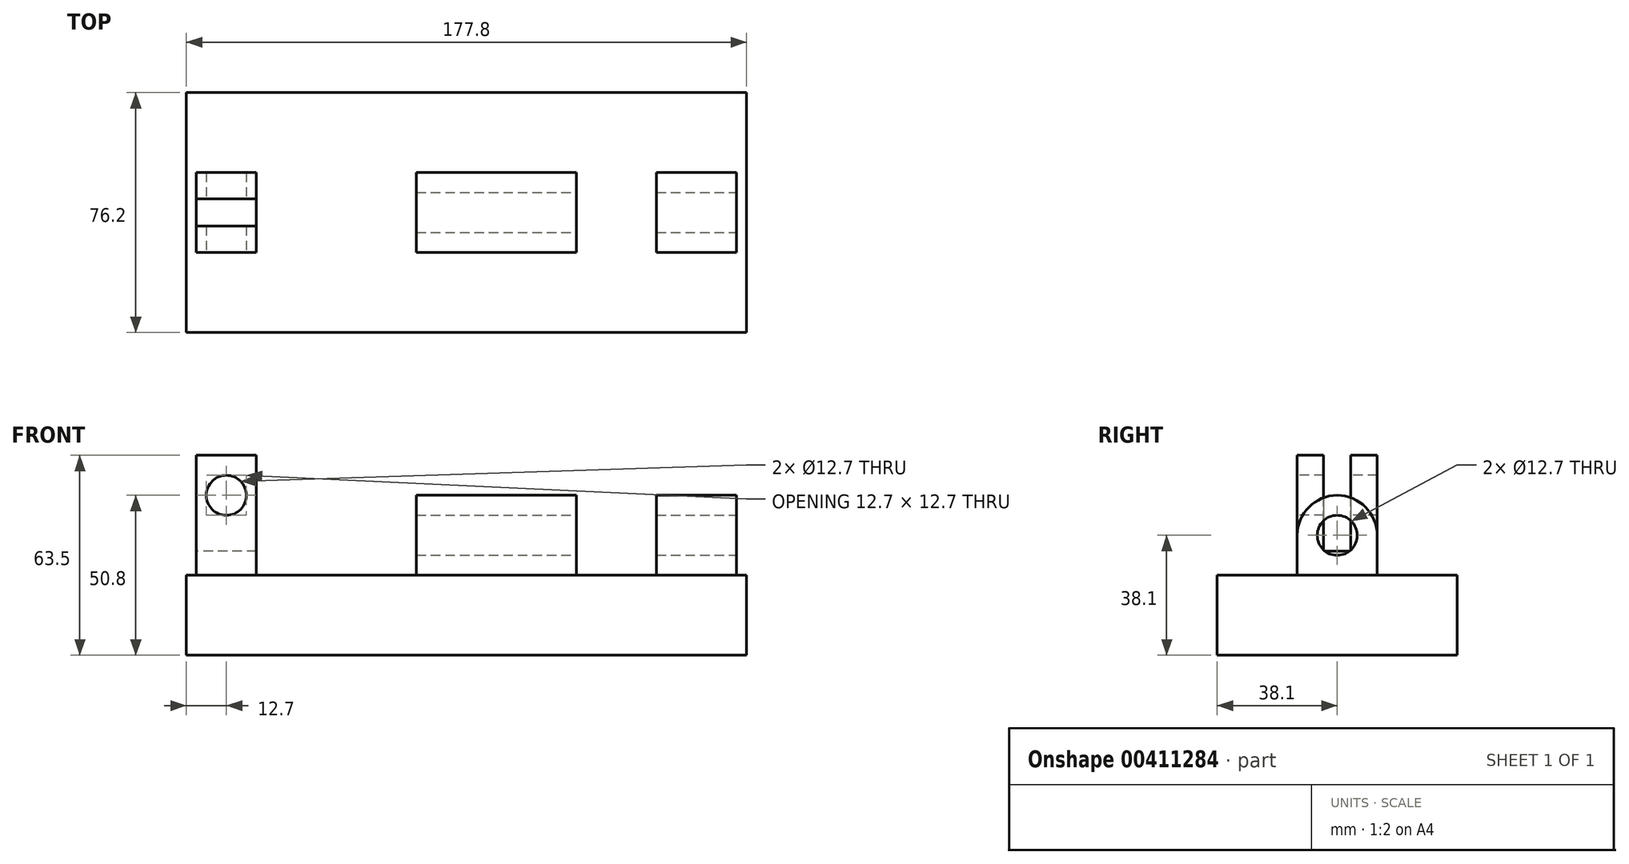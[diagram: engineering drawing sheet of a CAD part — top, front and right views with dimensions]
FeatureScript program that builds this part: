
annotation { "Feature Type Name" : "Feature", "Feature Type Description" : "" }
export const myFeature = defineFeature(function(context is Context, id is Id, definition is map)
    precondition{}
    {
        {
            var Q0;
            Q0=qCreatedBy(makeId("Top.planeOp"),FACE);
            var sketch = newSketch(context, id + "F0", { "sketchPlane" : qUnion([Q0])});
            skLineSegment(sketch, "E0.bottom", {"start": v(-88.9, 25.4) * mm, "end": v(88.9, 25.4) * mm});
            skLineSegment(sketch, "E0.top", {"start": v(-88.9, -50.8) * mm, "end": v(88.9, -50.8) * mm});
            skLineSegment(sketch, "E0.left", {"start": v(-88.9, 25.4) * mm, "end": v(-88.9, -50.8) * mm});
            skLineSegment(sketch, "E0.right", {"start": v(88.9, 25.4) * mm, "end": v(88.9, -50.8) * mm});
            skSolve(sketch);
        }
        {
            var Q0;
            Q0=makeQuery(id+"F0.imprint","IMPRINT",FACE,{"disambiguationData":[TD([[makeQuery(id+"F0.imprint","IMPRINT",EDGE,{"derivedFrom":sQuery(id+"F0.wireOp",EDGE,"E0.bottom")}),-1.0]])]});
            extrude(context, id + "F1", {"entities" : qUnion([Q0]), "depth" : 25.4 * mm});
        }
        {
            var Q0;
            Q0=qCreatedBy(makeId("Front.planeOp"),FACE);
            var sketch = newSketch(context, id + "F2", { "sketchPlane" : qUnion([Q0])});
            skLineSegment(sketch, "E1.bottom", {"start": v(-85.73, 63.5) * mm, "end": v(-66.68, 63.5) * mm});
            skLineSegment(sketch, "E1.top", {"start": v(-85.73, 25.4) * mm, "end": v(-66.68, 25.4) * mm});
            skLineSegment(sketch, "E1.left", {"start": v(-85.73, 63.5) * mm, "end": v(-85.73, 25.4) * mm});
            skLineSegment(sketch, "E1.right", {"start": v(-66.68, 63.5) * mm, "end": v(-66.68, 25.4) * mm});
            skLineSegment(sketch, "E2.bottom", {"start": v(-15.88, 50.8) * mm, "end": v(34.93, 50.8) * mm});
            skLineSegment(sketch, "E2.top", {"start": v(-15.88, 25.4) * mm, "end": v(34.93, 25.4) * mm});
            skLineSegment(sketch, "E2.left", {"start": v(-15.88, 50.8) * mm, "end": v(-15.88, 25.4) * mm});
            skLineSegment(sketch, "E2.right", {"start": v(34.93, 50.8) * mm, "end": v(34.93, 25.4) * mm});
            skLineSegment(sketch, "E3.bottom", {"start": v(60.33, 50.8) * mm, "end": v(85.72, 50.8) * mm});
            skLineSegment(sketch, "E3.top", {"start": v(60.32, 25.4) * mm, "end": v(85.73, 25.4) * mm});
            skLineSegment(sketch, "E3.left", {"start": v(85.73, 50.8) * mm, "end": v(85.73, 25.4) * mm});
            skLineSegment(sketch, "E3.right", {"start": v(60.33, 50.8) * mm, "end": v(60.33, 25.4) * mm});
            skSolve(sketch);
        }
        {
            var Q0;
            Q0 = qSketchRegion(id + "F2", true);
            extrude(context, id + "F3", {"entities" : qUnion([Q0]), "operationType" : NewBodyOperationType.ADD, "depth" : 25.4 * mm});
        }
        {
            var Q0;
            Q0=makeQuery(id+"F3.opExtrude","SWEPT_FACE",FACE,{"disambiguationData":[OSD([sQuery(id+"F2.wireOp",EDGE,"E3.left")])]});
            var sketch = newSketch(context, id + "F4", { "sketchPlane" : qUnion([Q0])});
            skCircle(sketch, "E4", {"center": v(-12.7, 38.1) * mm, "radius": 6.35 * mm});
            skPoint(sketch, "E4.centerSnap0", {"position": v(-12.7, 50.8) * mm});
            skPoint(sketch, "E4.centerSnap1", {"position": v(0, 38.1) * mm});
            skSolve(sketch);
        }
        {
            var Q0;
            Q0 = qSketchRegion(id + "F4", true);
            var Q1;
            Q1=makeQuery(id+"F3.opExtrude","SWEPT_FACE",FACE,{"disambiguationData":[OSD([sQuery(id+"F2.wireOp",EDGE,"E2.left")])]});
            extrude(context, id + "F5", {"entities" : qUnion([Q0]), "operationType" : NewBodyOperationType.REMOVE, "endBound" : BoundingType.UP_TO_SURFACE, "oppositeDirection" : true, "endBoundEntityFace" : qUnion([Q1]), "depth" : 25.4 * mm});
        }
        {
            var Q0;
            Q0=makeQuery(id+"F3.opExtrude","CAP_EDGE",EDGE,{"disambiguationData":[OSD([sQuery(id+"F2.wireOp",EDGE,"E2.bottom")])],"isStart":false});
            var Q1;
            Q1=makeQuery(id+"F3.opExtrude","CAP_EDGE",EDGE,{"disambiguationData":[OSD([sQuery(id+"F2.wireOp",EDGE,"E2.bottom")])],"isStart":true});
            var Q2;
            Q2=makeQuery(id+"F3.opExtrude","CAP_EDGE",EDGE,{"disambiguationData":[OSD([sQuery(id+"F2.wireOp",EDGE,"E3.bottom")])],"isStart":false});
            var Q3;
            Q3=makeQuery(id+"F3.opExtrude","CAP_EDGE",EDGE,{"disambiguationData":[OSD([sQuery(id+"F2.wireOp",EDGE,"E3.bottom")])],"isStart":true});
            fillet(context, id + "F6", {"entities" : qUnion([Q0, Q1, Q2, Q3]), "radius" : 12.7 * mm, "tangentPropagation" : true, "allowEdgeOverflow" : false});
        }
        {
            var Q0;
            Q0=makeQuery(id+"F3.opExtrude","SWEPT_FACE",FACE,{"disambiguationData":[OSD([sQuery(id+"F2.wireOp",EDGE,"E1.left")])]});
            var sketch = newSketch(context, id + "F7", { "sketchPlane" : qUnion([Q0])});
            skLineSegment(sketch, "E5.bottom", {"start": v(8.38, 63.5) * mm, "end": v(17.02, 63.5) * mm});
            skLineSegment(sketch, "E5.top", {"start": v(8.38, 33.02) * mm, "end": v(17.02, 33.02) * mm});
            skLineSegment(sketch, "E5.left", {"start": v(8.38, 63.5) * mm, "end": v(8.38, 33.02) * mm});
            skLineSegment(sketch, "E5.right", {"start": v(17.02, 63.5) * mm, "end": v(17.02, 33.02) * mm});
            skSolve(sketch);
        }
        {
            var Q0;
            Q0 = qSketchRegion(id + "F7", true);
            extrude(context, id + "F8", {"entities" : qUnion([Q0]), "operationType" : NewBodyOperationType.REMOVE, "oppositeDirection" : true, "depth" : 25.4 * mm});
        }
        {
            var Q0;
            Q0=makeQuery(id+"F3.opExtrude","CAP_FACE",FACE,{"disambiguationData":[OSD([sQuery(id+"F2.wireOp",EDGE,"E1.bottom"),sQuery(id+"F2.wireOp",EDGE,"E1.top"),sQuery(id+"F2.wireOp",EDGE,"E1.left"),sQuery(id+"F2.wireOp",EDGE,"E1.right")])],"isStart":false});
            var sketch = newSketch(context, id + "F9", { "sketchPlane" : qUnion([Q0])});
            skCircle(sketch, "E6", {"center": v(-76.2, 50.8) * mm, "radius": 6.35 * mm});
            skSolve(sketch);
        }
        {
            var Q0;
            Q0 = qSketchRegion(id + "F9", true);
            extrude(context, id + "F10", {"entities" : qUnion([Q0]), "operationType" : NewBodyOperationType.REMOVE, "oppositeDirection" : true, "depth" : 25.4 * mm});
        }
    });
